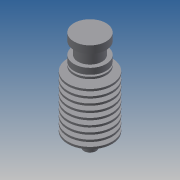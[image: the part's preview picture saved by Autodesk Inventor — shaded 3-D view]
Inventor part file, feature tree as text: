
AUTODESK INVENTOR PART (.ipt)
format: ipt  version: 2013 (Build 170138000, 138)  size: 171,520 bytes
history: native  units: mm
features: revolve x1, sketch x1
ambient origin geometry x8: Origin, YZ Plane, XZ Plane, XY Plane, X Axis, Y Axis, Z Axis, Center Point
bodies: Solid1 (feature_tree)
feature tree (2):
  revolve  "Revolution1"  [1 undecoded]
  sketch  "Sketch1"  dims[d0=3.7mm d2=6.0mm d3=3.0mm d4=8.0mm d5=6.0mm d6=3.0mm d7=49.8mm d8=90.0deg d9=1.0mm d11=26.0mm d12=7.1mm d13=11.0mm d14=5.0mm d15=2.05mm]
note: 1 required parameter value undecoded (feature->parameter linkage not recoverable at this tier; creation-order binding heuristic only, values carry confidence <= 0.55)
